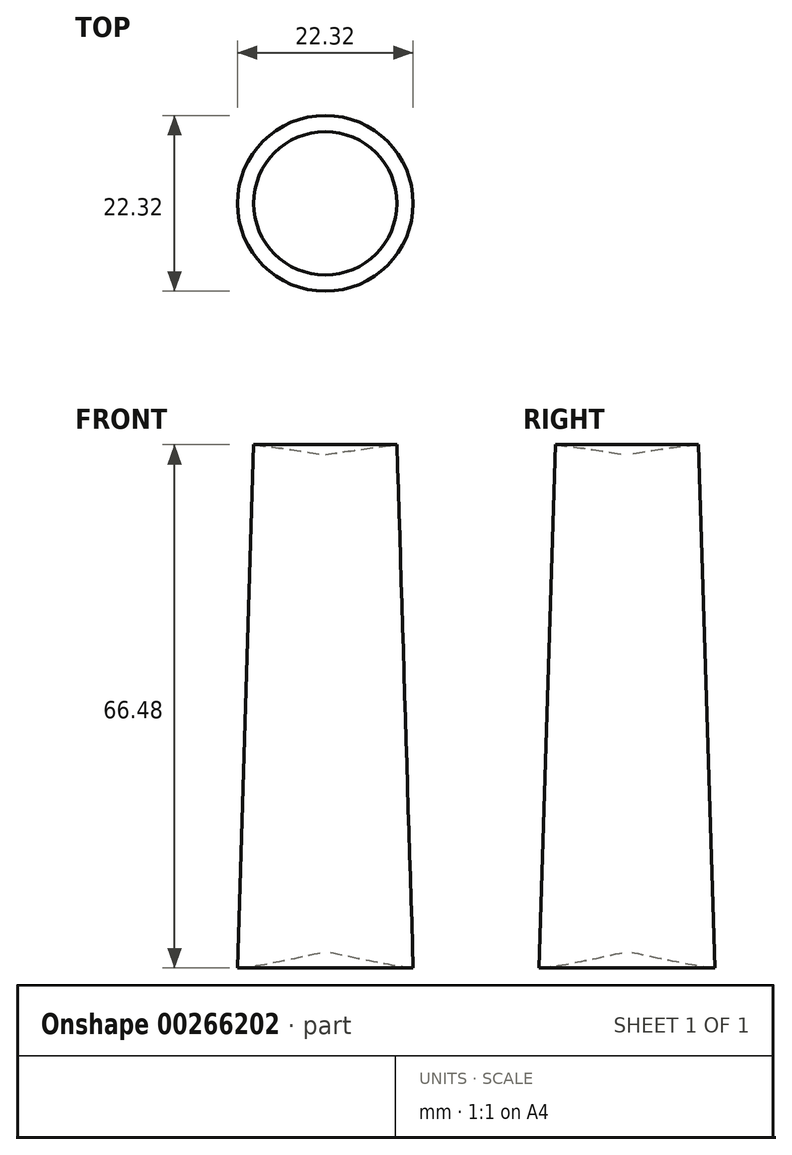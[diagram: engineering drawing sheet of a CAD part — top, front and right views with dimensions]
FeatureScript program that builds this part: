
annotation { "Feature Type Name" : "Feature", "Feature Type Description" : "" }
export const myFeature = defineFeature(function(context is Context, id is Id, definition is map)
    precondition{}
    {
        {
            var Q0;
            Q0=qCreatedBy(makeId("Front.planeOp"),FACE);
            var sketch = newSketch(context, id + "F0", { "sketchPlane" : qUnion([Q0])});
            skFitSpline(sketch, "E0", {"points": [v(0, 63.13) * mm, v(19.05, 62.94) * mm, v(18.68, 57.15) * mm, v(28.58, 53.41) * mm, v(25.19, 3.27) * mm, v(0, 0) * mm], "startDerivative": vector(138.62, 21.33) * mm, "endDerivative": vector(-147.36, 31.52) * mm});
            skLineSegment(sketch, "E1", {"start": v(0, 63.13) * mm, "end": v(0, 0) * mm});
            skLineSegment(sketch, "E2", {"start": v(9.1, 64.53) * mm, "end": v(11.17, -2.4) * mm});
            skSolve(sketch);
        }
        {
            var Q0;
            {var subQ0=sQuery(id+"F0.wireOp",EDGE,"E2");var subQ1=sQuery(id+"F0.wireOp",EDGE,"E0");var subQ2=makeQuery(id+"F0.imprint","INTERSECT",VERTEX,{"disambiguationData":[OD(0.0)],"derivedFrom":[subQ1,subQ0]});Q0=makeQuery(id+"F0.imprint","IMPRINT",FACE,{"disambiguationData":[TD([[makeQuery(id+"F0.imprint","IMPRINT",EDGE,{"disambiguationData":[TD([[subQ2,-1.0]])],"derivedFrom":subQ1}),-1.0]])]});}
            var Q1;
            Q1=sQuery(id+"F0.wireOp",EDGE,"E1");
            revolve(context, id + "F1", {"entities" : qUnion([Q0]), "axis" : qUnion([Q1]), "revolveType" : RevolveType.FULL});
        }
    });
